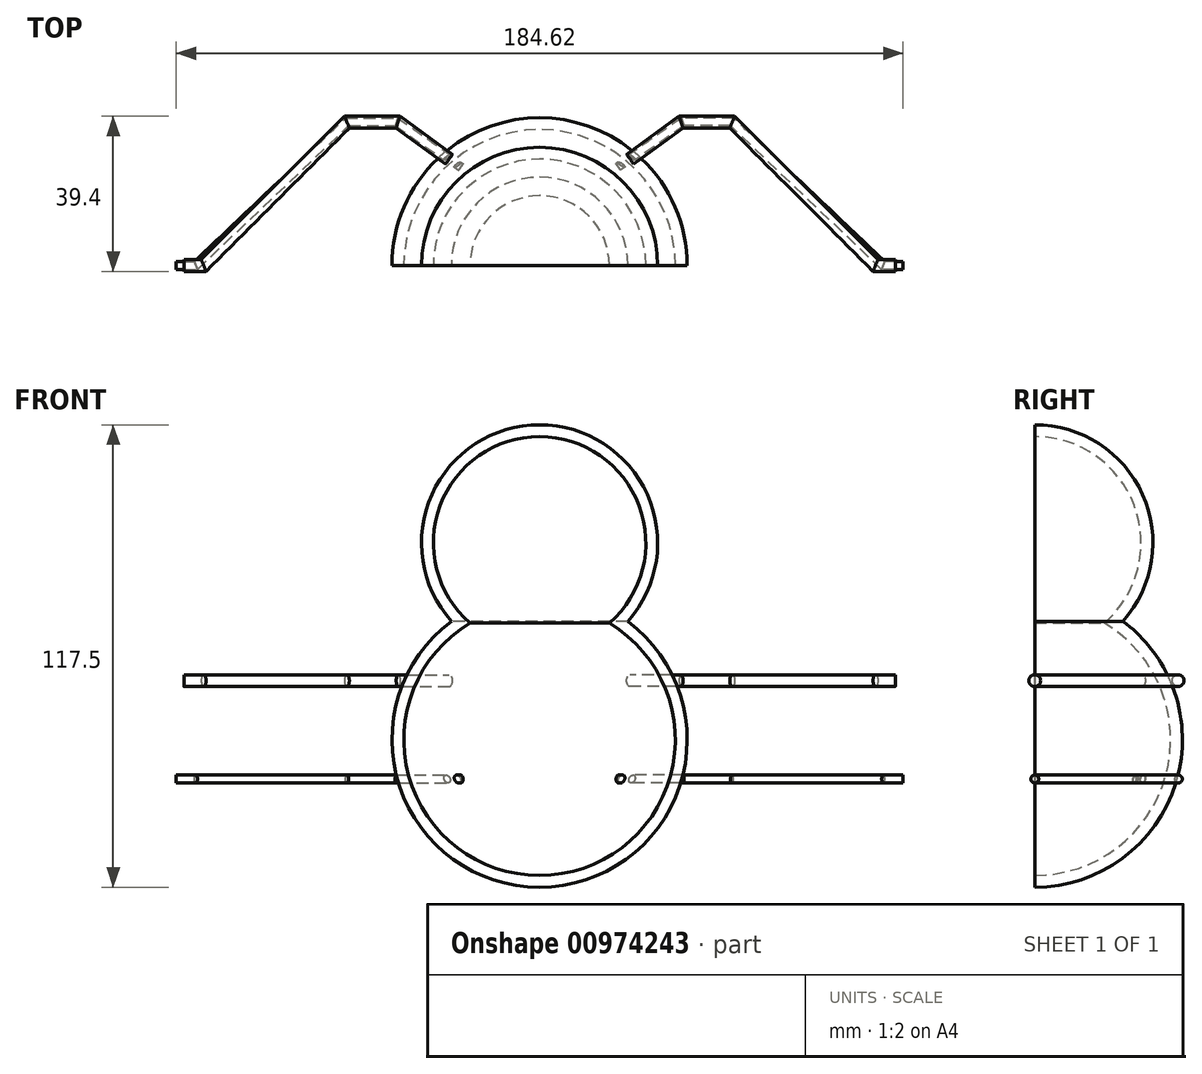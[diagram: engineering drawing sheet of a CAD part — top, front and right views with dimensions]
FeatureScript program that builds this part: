
annotation { "Feature Type Name" : "Feature", "Feature Type Description" : "" }
export const myFeature = defineFeature(function(context is Context, id is Id, definition is map)
    precondition{}
    {
        {
            var Q0;
            Q0=qCreatedBy(makeId("Front.planeOp"),FACE);
            var sketch = newSketch(context, id + "F0", { "sketchPlane" : qUnion([Q0])});
            skArc(sketch, "E0", {"start": v(0, 80) * mm, "mid": v(-27.37, 62.29) * mm, "end": v(-22.42, 30.06) * mm});
            skArc(sketch, "E1", {"start": v(-22.42, 30.06) * mm, "mid": v(-35.6, -11.8) * mm, "end": v(0, -37.5) * mm});
            skLineSegment(sketch, "E2", {"start": v(0, 80) * mm, "end": v(0, -37.5) * mm});
            skPoint(sketch, "E2.startSnap0", {"position": v(0, 80) * mm});
            skPoint(sketch, "E3.orphan", {"position": v(0, 83.68) * mm});
            skSolve(sketch);
        }
        {
            var Q0;
            Q0=makeQuery(id+"F0.imprint","IMPRINT",FACE,{"disambiguationData":[TD([[makeQuery(id+"F0.imprint","IMPRINT",EDGE,{"derivedFrom":sQuery(id+"F0.wireOp",EDGE,"E0")}),1.0]])]});
            var Q1;
            Q1=sQuery(id+"F0.wireOp",EDGE,"E2");
            revolve(context, id + "F1", {"surfaceOperationType" : NewSurfaceOperationType.NEW, "entities" : qUnion([Q0]), "axis" : qUnion([Q1]), "revolveType" : RevolveType.ONE_DIRECTION, "angle" : 180 * degree});
        }
        {
            var Q0;
            Q0=makeQuery(id+"F1.opRevolve","CAP_FACE",FACE,{"disambiguationData":[OSD([sQuery(id+"F0.wireOp",EDGE,"E0"),sQuery(id+"F0.wireOp",EDGE,"E1"),sQuery(id+"F0.wireOp",EDGE,"E2")])],"isStart":true});
            shell(context, id + "F2", {"entities" : qUnion([Q0]), "thickness" : 3 * mm});
        }
        {
            var Q0;
            Q0=qCreatedBy(makeId("Top.planeOp"),FACE);
            cPlane(context, id + "F3", {"entities" : qUnion([Q0]), "cplaneType" : CPlaneType.OFFSET, "offset" : 10 * mm, "oppositeDirection" : true, "width" : 152.4 * mm, "height" : 152.4 * mm});
        }
        {
            var Q0;
            Q0=qCreatedBy(id+"F3.planeOp",FACE);
            var sketch = newSketch(context, id + "F4", { "sketchPlane" : qUnion([Q0])});
            skLineSegment(sketch, "E4", {"start": v(-20, 25) * mm, "end": v(-36.38, 36.47) * mm});
            skLineSegment(sketch, "E5", {"start": v(-36.38, 36.47) * mm, "end": v(-48.88, 36.47) * mm});
            skLineSegment(sketch, "E6", {"start": v(-48.88, 36.47) * mm, "end": v(-87.3, 0) * mm});
            skLineSegment(sketch, "E7", {"start": v(-87.3, 0) * mm, "end": v(-92.3, 0) * mm});
            skPoint(sketch, "E8.center.orphan", {"position": v(0, 0) * mm});
            skSolve(sketch);
        }
        {
            var Q0;
            Q0=qCreatedBy(makeId("Right.planeOp"),FACE);
            var Q1;
            Q1=sQuery(id+"F4.wireOp",VERTEX,"E7.end");
            cPlane(context, id + "F5", {"entities" : qUnion([Q0, Q1]), "cplaneType" : CPlaneType.PLANE_POINT, "offset" : 25 * mm, "width" : 150 * mm, "height" : 150 * mm});
        }
        {
            var Q0;
            Q0=qCreatedBy(id+"F5.planeOp",FACE);
            var sketch = newSketch(context, id + "F6", { "sketchPlane" : qUnion([Q0])});
            skCircle(sketch, "E9", {"center": v(0, -10) * mm, "radius": 1 * mm});
            skSolve(sketch);
        }
        {
            var Q0;
            Q0=makeQuery(id+"F6.imprint","IMPRINT",FACE,{"disambiguationData":[TD([[makeQuery(id+"F6.imprint","IMPRINT",EDGE,{"derivedFrom":sQuery(id+"F6.wireOp",EDGE,"E9")}),1.0]])]});
            var Q1;
            Q1=sQuery(id+"F4.wireOp",EDGE,"E7");
            var Q2;
            Q2=sQuery(id+"F4.wireOp",EDGE,"E6");
            var Q3;
            Q3=sQuery(id+"F4.wireOp",EDGE,"E5");
            var Q4;
            Q4=sQuery(id+"F4.wireOp",EDGE,"E4");
            sweep(context, id + "F7", {"profiles" : qUnion([Q0]), "path" : qUnion([Q1, Q2, Q3, Q4])});
        }
        {
            var Q0;
            Q0=makeQuery(id+"F7.opSweep","SWEPT_BODY",BODY,{"disambiguationData":[OSD([sQuery(id+"F4.wireOp",EDGE,"E4"),sQuery(id+"F6.wireOp",EDGE,"E9")])]});
            var Q1;
            Q1=qCreatedBy(makeId("Right.planeOp"),FACE);
            mirror(context, id + "F8", {"operationType" : NewBodyOperationType.ADD, "entities" : qUnion([Q0]), "mirrorPlane" : qUnion([Q1])});
        }
        {
            var Q0;
            Q0=qCreatedBy(makeId("Top.planeOp"),FACE);
            cPlane(context, id + "F9", {"entities" : qUnion([Q0]), "cplaneType" : CPlaneType.OFFSET, "offset" : 15 * mm, "width" : 150 * mm, "height" : 150 * mm});
        }
        {
            var Q0;
            Q0=qCreatedBy(id+"F9.planeOp",FACE);
            var sketch = newSketch(context, id + "F10", { "sketchPlane" : qUnion([Q0])});
            skLineSegment(sketch, "E10", {"start": v(23, 27) * mm, "end": v(35.94, 36.4) * mm});
            skLineSegment(sketch, "E11", {"start": v(35.94, 36.4) * mm, "end": v(48.94, 36.4) * mm});
            skLineSegment(sketch, "E12", {"start": v(48.94, 36.4) * mm, "end": v(85.35, 0) * mm});
            skLineSegment(sketch, "E13", {"start": v(85.35, 0) * mm, "end": v(90.35, 0) * mm});
            skSolve(sketch);
        }
        {
            var Q0;
            Q0=sQuery(id+"F10.wireOp",VERTEX,"E13.end");
            var Q1;
            Q1=qCreatedBy(makeId("Right.planeOp"),FACE);
            cPlane(context, id + "F11", {"entities" : qUnion([Q0, Q1]), "cplaneType" : CPlaneType.PLANE_POINT, "offset" : 25 * mm, "width" : 150 * mm, "height" : 150 * mm});
        }
        {
            var Q0;
            Q0=qCreatedBy(id+"F11.planeOp",FACE);
            var sketch = newSketch(context, id + "F12", { "sketchPlane" : qUnion([Q0])});
            skCircle(sketch, "E14", {"center": v(0, 15) * mm, "radius": 1.5 * mm});
            skSolve(sketch);
        }
        {
            var Q0;
            Q0=makeQuery(id+"F12.imprint","IMPRINT",FACE,{"disambiguationData":[TD([[makeQuery(id+"F12.imprint","IMPRINT",EDGE,{"derivedFrom":sQuery(id+"F12.wireOp",EDGE,"E14")}),1.0]])]});
            var Q1;
            Q1=sQuery(id+"F10.wireOp",EDGE,"E13");
            var Q2;
            Q2=sQuery(id+"F10.wireOp",EDGE,"E12");
            var Q3;
            Q3=sQuery(id+"F10.wireOp",EDGE,"E11");
            var Q4;
            Q4=sQuery(id+"F10.wireOp",EDGE,"E10");
            sweep(context, id + "F13", {"profiles" : qUnion([Q0]), "path" : qUnion([Q1, Q2, Q3, Q4])});
        }
        {
            var Q0;
            Q0=makeQuery(id+"F13.opSweep","SWEPT_BODY",BODY,{"disambiguationData":[OSD([sQuery(id+"F10.wireOp",EDGE,"E10"),sQuery(id+"F12.wireOp",EDGE,"E14")])]});
            var Q1;
            Q1=qCreatedBy(makeId("Right.planeOp"),FACE);
            mirror(context, id + "F14", {"entities" : qUnion([Q0]), "mirrorPlane" : qUnion([Q1])});
        }
    });
